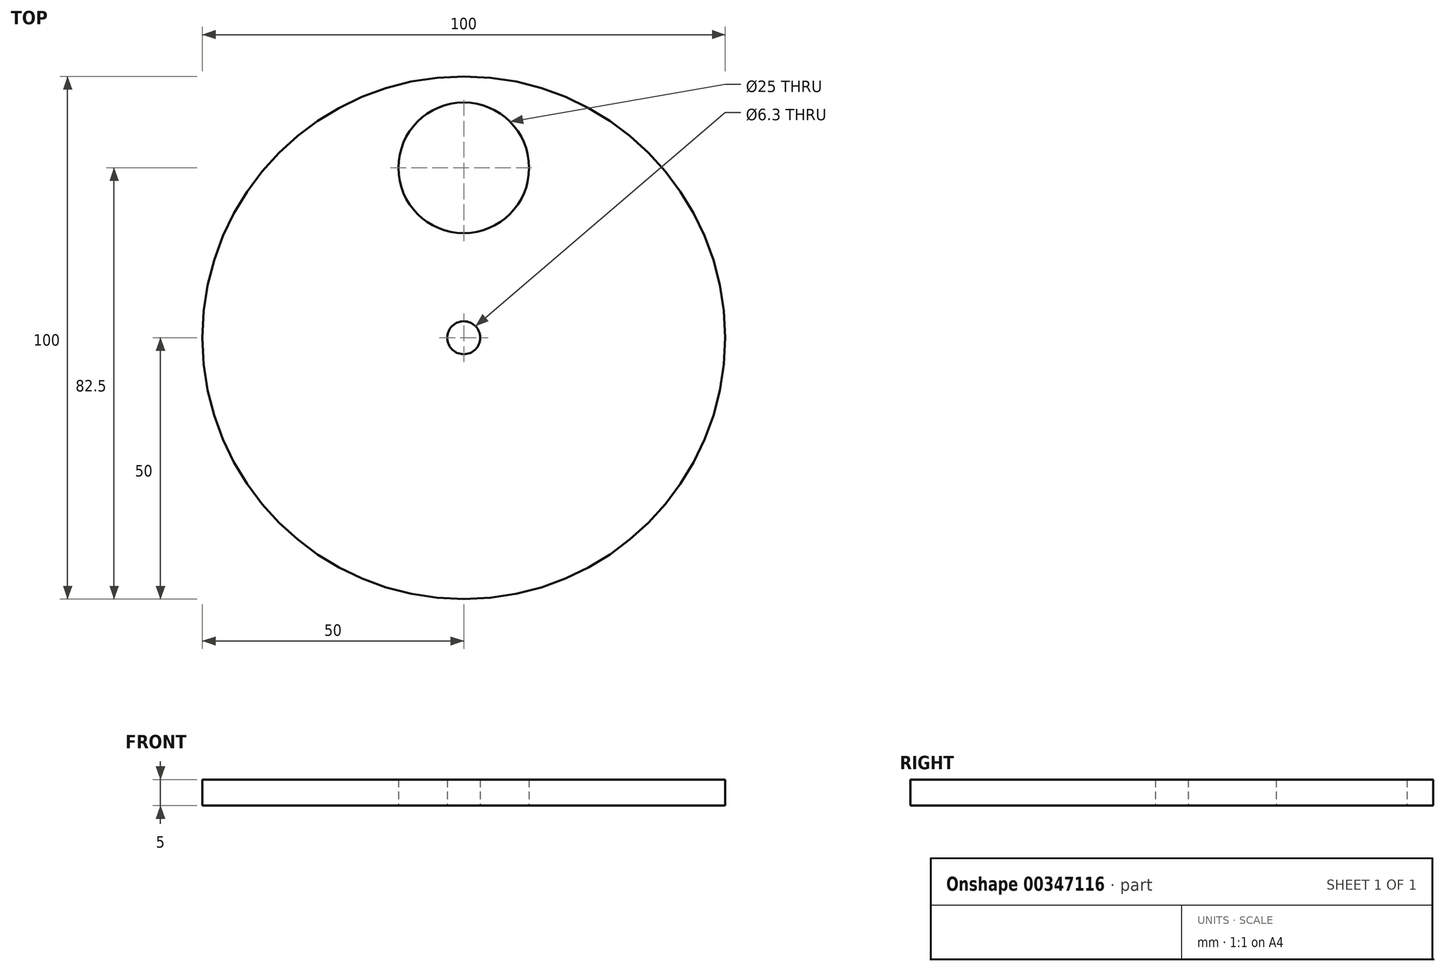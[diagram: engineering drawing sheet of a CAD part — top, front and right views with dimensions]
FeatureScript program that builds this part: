
annotation { "Feature Type Name" : "Feature", "Feature Type Description" : "" }
export const myFeature = defineFeature(function(context is Context, id is Id, definition is map)
    precondition{}
    {
        {
            var Q0;
            Q0=qCreatedBy(makeId("Top.planeOp"),FACE);
            var sketch = newSketch(context, id + "F0", { "sketchPlane" : qUnion([Q0])});
            skCircle(sketch, "E0", {"center": v(0, 0) * mm, "radius": 50 * mm});
            skCircle(sketch, "E1", {"center": v(0, 32.5) * mm, "radius": 12.5 * mm});
            skCircle(sketch, "E2", {"center": v(0, 0) * mm, "radius": 3.15 * mm});
            skSolve(sketch);
        }
        {
            var Q0;
            Q0=makeQuery(id+"F0.imprint","IMPRINT",FACE,{"disambiguationData":[TD([[makeQuery(id+"F0.imprint","IMPRINT",EDGE,{"derivedFrom":sQuery(id+"F0.wireOp",EDGE,"E0")}),1.0]])]});
            extrude(context, id + "F1", {"entities" : qUnion([Q0]), "depth" : 5 * mm});
        }
    });
